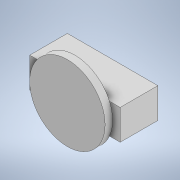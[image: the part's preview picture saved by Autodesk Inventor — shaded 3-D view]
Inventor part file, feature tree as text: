
AUTODESK INVENTOR PART (.ipt)
format: ipt  version: 2020.1 (Build 241239000, 239)  size: 111,616 bytes
history: native  units: mm
features: extrude x2, sketch x2
ambient origin geometry x8: Origin, YZ Plane, XZ Plane, XY Plane, X Axis, Y Axis, Z Axis, Center Point
bodies: Solid1 (feature_tree)
feature tree (4):
  extrude  "Extrusion1"  Depth=4.0mm
  extrude  "Extrusion3"  Depth=10.0mm
  sketch  "Sketch1"  dims[d2=2.0mm d3=4.0mm]
  sketch  "Sketch2"  dims[d4=5.0mm d5=0.0mm d9=10.0mm d10=1.0mm d11=0.0mm]
